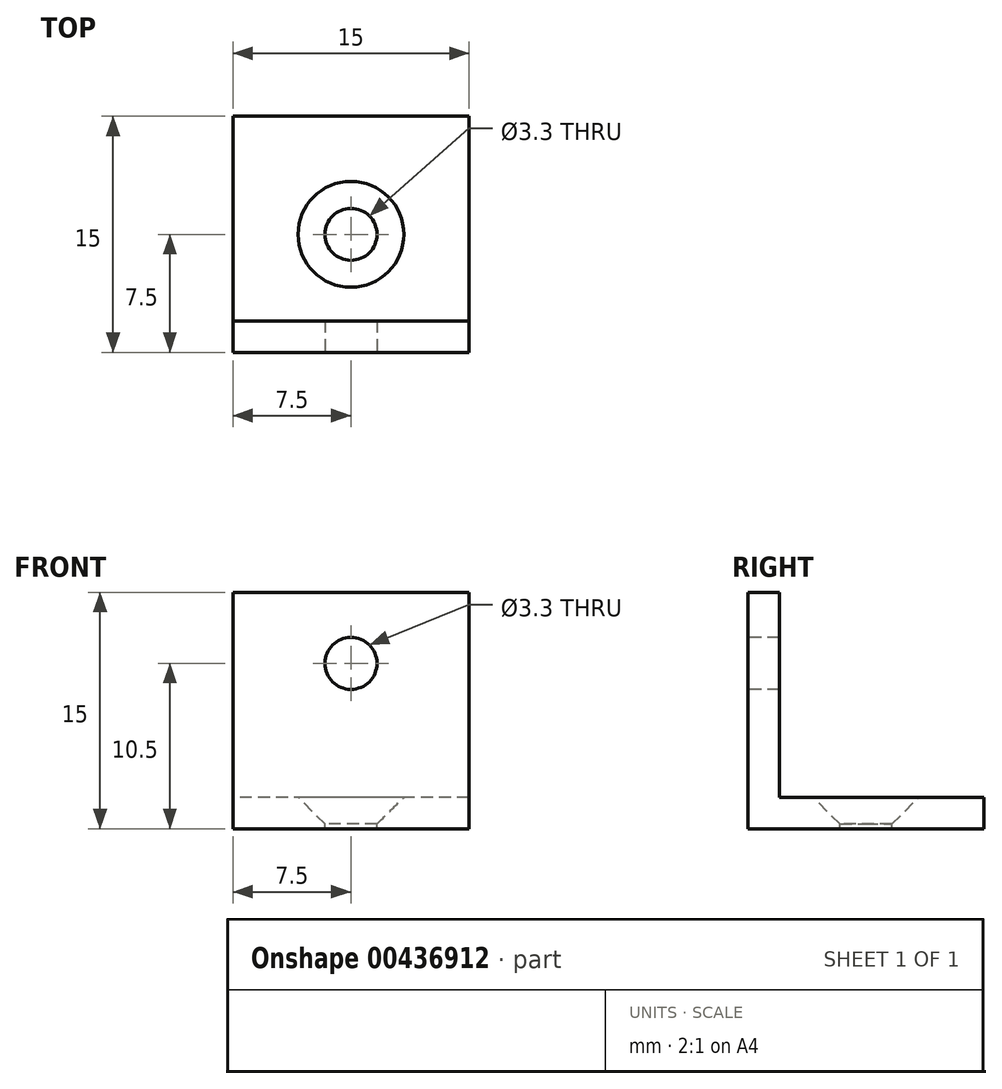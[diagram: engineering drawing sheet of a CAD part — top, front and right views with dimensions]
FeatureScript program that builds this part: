
annotation { "Feature Type Name" : "Feature", "Feature Type Description" : "" }
export const myFeature = defineFeature(function(context is Context, id is Id, definition is map)
    precondition{}
    {
        {
            var Q0;
            Q0=qCreatedBy(makeId("Right.planeOp"),FACE);
            var sketch = newSketch(context, id + "F0", { "sketchPlane" : qUnion([Q0])});
            skLineSegment(sketch, "E0", {"start": v(0, 0) * mm, "end": v(15, 0) * mm});
            skLineSegment(sketch, "E1", {"start": v(15, 0) * mm, "end": v(15, 2) * mm});
            skLineSegment(sketch, "E2", {"start": v(15, 2) * mm, "end": v(2, 2) * mm});
            skLineSegment(sketch, "E3", {"start": v(2, 2) * mm, "end": v(2, 15) * mm});
            skLineSegment(sketch, "E4", {"start": v(2, 15) * mm, "end": v(0, 15) * mm});
            skLineSegment(sketch, "E5", {"start": v(0, 15) * mm, "end": v(0, 0) * mm});
            skSolve(sketch);
        }
        {
            var Q0;
            Q0=qSketchRegion(id+"F0",true);
            extrude(context, id + "F1", {"entities" : qUnion([Q0]), "depth" : 15 * mm});
        }
        {
            var Q0;
            Q0=makeQuery(id+"F1.opExtrude","SWEPT_FACE",FACE,{"disambiguationData":[OSD([sQuery(id+"F0.wireOp",EDGE,"E5")])]});
            var sketch = newSketch(context, id + "F2", { "sketchPlane" : qUnion([Q0])});
            skPoint(sketch, "E6", {"position": v(7.5, 10.5) * mm});
            skSolve(sketch);
        }
        {
            var Q0;
            Q0=sQuery(id+"F2.wireOp",VERTEX,"E6");
            var Q1;
            Q1=makeQuery(id+"F1.opExtrude","SWEPT_BODY",BODY,{"disambiguationData":[OSD([sQuery(id+"F0.wireOp",EDGE,"E0"),sQuery(id+"F0.wireOp",EDGE,"E1"),sQuery(id+"F0.wireOp",EDGE,"E2"),sQuery(id+"F0.wireOp",EDGE,"E3"),sQuery(id+"F0.wireOp",EDGE,"E4"),sQuery(id+"F0.wireOp",EDGE,"E5")])]});
            hole(context, id + "F3", {"style" : HoleStyle.SIMPLE, "endStyle" : HoleEndStyle.THROUGH, "standardTappedOrClearance" : lookupTablePath({ "standard" : "ISO", "engagement" : "75%", "pitch" : "0.7 mm", "size" : "M4", "type" : "Tapped" }), "standardBlindInLast" : lookupTablePath({ "standard" : "ISO", "engagement" : "75%", "pitch" : "0.7 mm", "size" : "M4", "type" : "Tapped" }), "holeDiameter" : 3.3 * mm, "showTappedDepth" : true, "isTappedThrough" : true, "tappedDepth" : 12 * mm, "tapClearance" : 3, "locations" : qUnion([Q0]), "scope" : qUnion([Q1]), "majorDiameter" : 4 * mm});
        }
        {
            var Q0;
            Q0=makeQuery(id+"F1.opExtrude","SWEPT_FACE",FACE,{"disambiguationData":[OSD([sQuery(id+"F0.wireOp",EDGE,"E2")])]});
            var sketch = newSketch(context, id + "F4", { "sketchPlane" : qUnion([Q0])});
            skPoint(sketch, "E7", {"position": v(7.5, 7.5) * mm});
            skSolve(sketch);
        }
        {
            var Q0;
            Q0=sQuery(id+"F4.wireOp",VERTEX,"E7");
            var Q1;
            Q1=makeQuery(id+"F1.opExtrude","SWEPT_BODY",BODY,{"disambiguationData":[OSD([sQuery(id+"F0.wireOp",EDGE,"E0"),sQuery(id+"F0.wireOp",EDGE,"E1"),sQuery(id+"F0.wireOp",EDGE,"E2"),sQuery(id+"F0.wireOp",EDGE,"E3"),sQuery(id+"F0.wireOp",EDGE,"E4"),sQuery(id+"F0.wireOp",EDGE,"E5")])]});
            hole(context, id + "F5", {"style" : HoleStyle.C_SINK, "endStyle" : HoleEndStyle.THROUGH, "standardTappedOrClearance" : lookupTablePath({ "standard" : "ISO", "fit" : "Normal", "size" : "M3", "type" : "Clearance" }), "standardBlindInLast" : lookupTablePath({ "fit" : "Standard", "standard" : "ISO", "size" : "M3", "type" : "Clearance" }), "holeDiameter" : 3.3 * mm, "cSinkDiameter" : 6.72 * mm, "cSinkAngle" : 90 * degree, "isTappedThrough" : true, "tappedDepth" : 12 * mm, "tapClearance" : 3, "locations" : qUnion([Q0]), "scope" : qUnion([Q1])});
        }
    });
